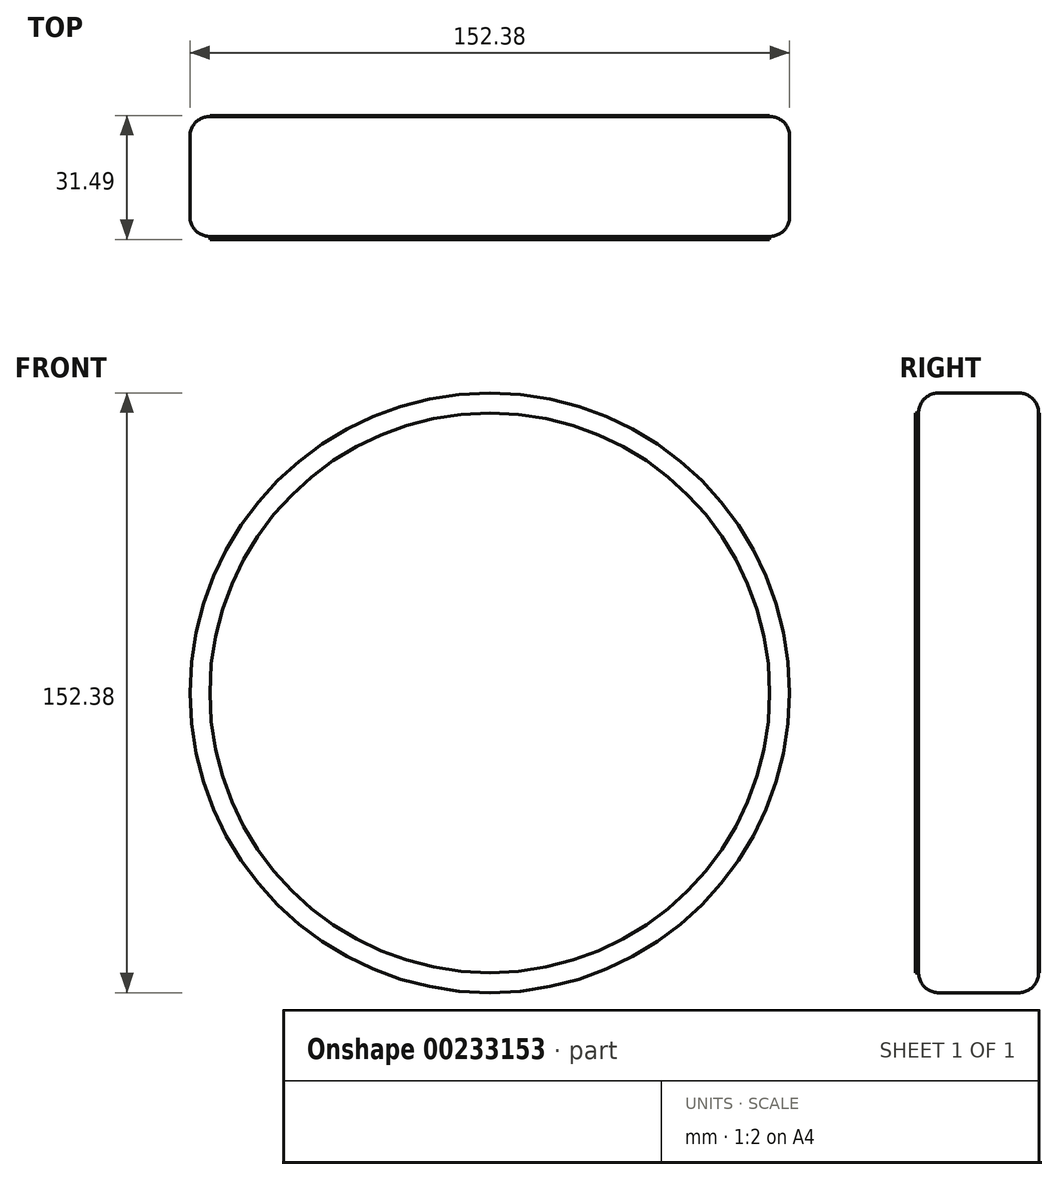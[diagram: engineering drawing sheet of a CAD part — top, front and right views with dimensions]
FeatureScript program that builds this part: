
annotation { "Feature Type Name" : "Feature", "Feature Type Description" : "" }
export const myFeature = defineFeature(function(context is Context, id is Id, definition is map)
    precondition{}
    {
        {
            var Q0;
            Q0=qCreatedBy(makeId("Front.planeOp"),FACE);
            var sketch = newSketch(context, id + "F0", { "sketchPlane" : qUnion([Q0])});
            skCircle(sketch, "E0", {"center": v(0, 0) * mm, "radius": 76.2 * mm});
            skSolve(sketch);
        }
        {
            var Q0;
            Q0=makeQuery(id+"F0.imprint","IMPRINT",FACE,{"disambiguationData":[TD([[makeQuery(id+"F0.imprint","IMPRINT",EDGE,{"derivedFrom":sQuery(id+"F0.wireOp",EDGE,"E0")}),1.0]])]});
            extrude(context, id + "F1", {"entities" : qUnion([Q0]), "depth" : 15.24 * mm});
        }
        {
            var Q0;
            Q0=makeQuery(id+"F1.opExtrude","CAP_FACE",FACE,{"disambiguationData":[OSD([sQuery(id+"F0.wireOp",EDGE,"E0")])],"isStart":true});
            extrude(context, id + "F2", {"entities" : qUnion([Q0]), "operationType" : NewBodyOperationType.ADD, "depth" : 15.24 * mm});
        }
        {
            var Q0;
            {var subQ0=sQuery(id+"F0.wireOp",EDGE,"E0");Q0=makeQuery(id+"F2.boolean.opBoolean","MERGE",FACE,{"derivedFrom":[makeQuery(id+"F1.opExtrude","SWEPT_FACE",FACE,{"disambiguationData":[OSD([subQ0])]}),makeQuery(id+"F2.opExtrude","SWEPT_FACE",FACE,{"disambiguationData":[OSD([subQ0])]})]});}
            fillet(context, id + "F3", {"entities" : qUnion([Q0]), "radius" : 5.08 * mm, "tangentPropagation" : true, "allowEdgeOverflow" : false});
        }
        {
            var Q0;
            Q0=makeQuery(id+"F1.opExtrude","CAP_FACE",FACE,{"disambiguationData":[OSD([sQuery(id+"F0.wireOp",EDGE,"E0")])],"isStart":false});
            var sketch = newSketch(context, id + "F4", { "sketchPlane" : qUnion([Q0])});
            skLineSegment(sketch, "E1", {"start": v(0, 0) * mm, "end": v(0, 71.11) * mm});
            skLineSegment(sketch, "E2.1.0", {"start": v(0, 0) * mm, "end": v(61.59, -35.56) * mm});
            skLineSegment(sketch, "E2.2.0", {"start": v(0, 0) * mm, "end": v(-61.59, -35.56) * mm});
            skPoint(sketch, "E2.center", {"position": v(0, 0) * mm});
            skLineSegment(sketch, "E2.anchor1", {"start": v(0, 0) * mm, "end": v(0, 71.11) * mm, "construction": true});
            skLineSegment(sketch, "E2.anchor2", {"start": v(0, 0) * mm, "end": v(-61.59, -35.56) * mm, "construction": true});
            skSolve(sketch);
        }
        {
            var Q0;
            {var subQ0=sQuery(id+"F4.wireOp",EDGE,"E2.1.0");Q0=makeQuery(id+"F4.imprint","IMPRINT",FACE,{"disambiguationData":[TD([[makeQuery(id+"F4.imprint","IMPRINT",EDGE,{"derivedFrom":subQ0}),-1.0]])]});}
            var Q1;
            {var subQ0=sQuery(id+"F4.wireOp",EDGE,"E1");Q1=makeQuery(id+"F4.imprint","IMPRINT",FACE,{"disambiguationData":[TD([[makeQuery(id+"F4.imprint","IMPRINT",EDGE,{"derivedFrom":subQ0}),1.0]])]});}
            var Q2;
            {var subQ0=sQuery(id+"F4.wireOp",EDGE,"E1");Q2=makeQuery(id+"F4.imprint","IMPRINT",FACE,{"disambiguationData":[TD([[makeQuery(id+"F4.imprint","IMPRINT",EDGE,{"derivedFrom":subQ0}),-1.0]])]});}
            extrude(context, id + "F5", {"entities" : qUnion([Q0, Q1, Q2]), "operationType" : NewBodyOperationType.ADD, "depth" : 0.76 * mm});
        }
        {
            var Q0;
            Q0=makeQuery(id+"F2.opExtrude","CAP_FACE",FACE,{"disambiguationData":[OSD([sQuery(id+"F0.wireOp",EDGE,"E0")])],"isStart":false});
            var sketch = newSketch(context, id + "F6", { "sketchPlane" : qUnion([Q0])});
            skSolve(sketch);
        }
        {
            var Q0;
            {var subQ0=sQuery(id+"F0.wireOp",EDGE,"E0");Q0=makeQuery(id+"F6.imprint","IMPRINT",FACE,{"disambiguationData":[TD([[makeQuery(id+"F6.imprint","IMPRINT",EDGE,{"derivedFrom":makeQuery(id+"F3.opFillet","BLEND_EDGE",EDGE,{"blendedFrom":[makeQuery(id+"F2.opExtrude","CAP_EDGE",EDGE,{"disambiguationData":[OSD([subQ0])],"isStart":false}),makeQuery(id+"F2.opExtrude","CAP_FACE",FACE,{"disambiguationData":[OSD([subQ0])],"isStart":false})],"blendedInto":[makeQuery(id+"F2.opExtrude","CAP_FACE",FACE,{"disambiguationData":[OSD([subQ0])],"isStart":false})]})}),1.0]])]});}
            extrude(context, id + "F7", {"entities" : qUnion([Q0]), "operationType" : NewBodyOperationType.ADD, "depth" : 0.25 * mm});
        }
    });
